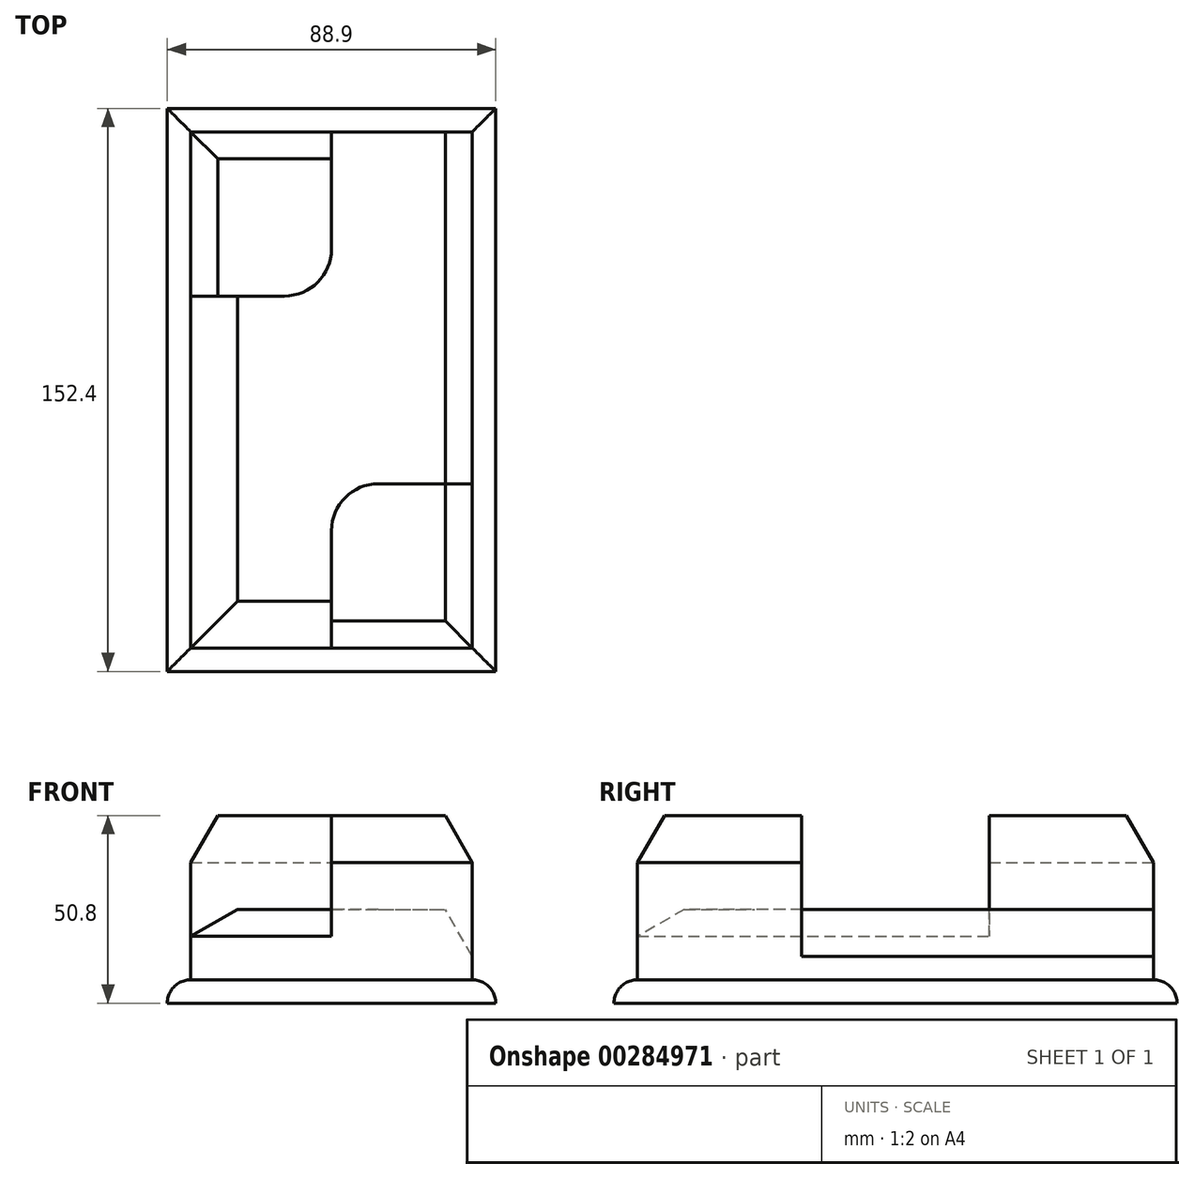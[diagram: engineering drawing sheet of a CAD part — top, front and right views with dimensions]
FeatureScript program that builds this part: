
annotation { "Feature Type Name" : "Feature", "Feature Type Description" : "" }
export const myFeature = defineFeature(function(context is Context, id is Id, definition is map)
    precondition{}
    {
        {
            var Q0;
            Q0=qCreatedBy(makeId("Top.planeOp"),FACE);
            var sketch = newSketch(context, id + "F0", { "sketchPlane" : qUnion([Q0])});
            skLineSegment(sketch, "E0.bottom", {"start": v(-50.87, 68.07) * mm, "end": v(25.33, 68.07) * mm});
            skLineSegment(sketch, "E0.top", {"start": v(-50.87, -71.63) * mm, "end": v(25.33, -71.63) * mm});
            skLineSegment(sketch, "E0.left", {"start": v(-50.87, 68.07) * mm, "end": v(-50.87, -71.63) * mm});
            skLineSegment(sketch, "E0.right", {"start": v(25.33, 68.07) * mm, "end": v(25.33, -71.63) * mm});
            skLineSegment(sketch, "E1.0", {"start": v(-57.22, 74.42) * mm, "end": v(31.68, 74.42) * mm});
            skLineSegment(sketch, "E1.1", {"start": v(-57.22, 74.42) * mm, "end": v(-57.22, -77.98) * mm});
            skLineSegment(sketch, "E1.2", {"start": v(-57.22, -77.98) * mm, "end": v(31.68, -77.98) * mm});
            skLineSegment(sketch, "E1.3", {"start": v(31.68, 74.42) * mm, "end": v(31.68, -77.98) * mm});
            skPoint(sketch, "E2", {"position": v(-12.77, 68.07) * mm});
            skLineSegment(sketch, "E3", {"start": v(-12.77, 68.07) * mm, "end": v(-12.77, 36.32) * mm});
            skLineSegment(sketch, "E4", {"start": v(-25.47, 23.62) * mm, "end": v(-50.87, 23.62) * mm});
            skPoint(sketch, "E5.visualSharp", {"position": v(-12.77, 23.62) * mm});
            skArc(sketch, "E5.filletArc", {"start": v(-25.47, 23.62) * mm, "mid": v(-16.5, 27.34) * mm, "end": v(-12.77, 36.32) * mm});
            skLineSegment(sketch, "E6", {"start": v(-12.77, -71.63) * mm, "end": v(-12.77, -39.88) * mm});
            skLineSegment(sketch, "E7", {"start": v(-0.07, -27.18) * mm, "end": v(25.33, -27.18) * mm});
            skPoint(sketch, "E8.visualSharp", {"position": v(-12.77, -27.18) * mm});
            skArc(sketch, "E8.filletArc", {"start": v(-0.07, -27.18) * mm, "mid": v(-9.05, -30.9) * mm, "end": v(-12.77, -39.88) * mm});
            skSolve(sketch);
        }
        {
            var Q0;
            Q0=makeQuery(id+"F0.imprint","IMPRINT",FACE,{"disambiguationData":[TD([[makeQuery(id+"F0.imprint","IMPRINT",EDGE,{"derivedFrom":sQuery(id+"F0.wireOp",EDGE,"E1.0")}),-1.0]])]});
            extrude(context, id + "F1", {"entities" : qUnion([Q0]), "depth" : 6.35 * mm});
        }
        {
            var Q0;
            {var subQ9=sQuery(id+"F0.wireOp",EDGE,"E3");Q0=makeQuery(id+"F0.imprint","IMPRINT",FACE,{"disambiguationData":[TD([[makeQuery(id+"F0.imprint","IMPRINT",EDGE,{"derivedFrom":subQ9}),1.0]])]});}
            extrude(context, id + "F2", {"entities" : qUnion([Q0]), "operationType" : NewBodyOperationType.ADD, "depth" : 25.4 * mm});
        }
        {
            var Q0;
            {var subQ1=sQuery(id+"F0.wireOp",EDGE,"E3");Q0=makeQuery(id+"F0.imprint","IMPRINT",FACE,{"disambiguationData":[TD([[makeQuery(id+"F0.imprint","IMPRINT",EDGE,{"derivedFrom":subQ1}),-1.0]])]});}
            var Q1;
            {var subQ1=sQuery(id+"F0.wireOp",EDGE,"E6");Q1=makeQuery(id+"F0.imprint","IMPRINT",FACE,{"disambiguationData":[TD([[makeQuery(id+"F0.imprint","IMPRINT",EDGE,{"derivedFrom":subQ1}),-1.0]])]});}
            extrude(context, id + "F3", {"entities" : qUnion([Q0, Q1]), "operationType" : NewBodyOperationType.ADD, "depth" : 50.8 * mm});
        }
        {
            var Q0;
            Q0=makeQuery(id+"F1.opExtrude","CAP_EDGE",EDGE,{"disambiguationData":[OSD([sQuery(id+"F0.wireOp",EDGE,"E1.3")])],"isStart":false});
            var Q1;
            Q1=makeQuery(id+"F1.opExtrude","CAP_EDGE",EDGE,{"disambiguationData":[OSD([sQuery(id+"F0.wireOp",EDGE,"E1.2")])],"isStart":false});
            var Q2;
            Q2=makeQuery(id+"F1.opExtrude","CAP_EDGE",EDGE,{"disambiguationData":[OSD([sQuery(id+"F0.wireOp",EDGE,"E1.1")])],"isStart":false});
            var Q3;
            Q3=makeQuery(id+"F1.opExtrude","CAP_EDGE",EDGE,{"disambiguationData":[OSD([sQuery(id+"F0.wireOp",EDGE,"E1.0")])],"isStart":false});
            fillet(context, id + "F4", {"entities" : qUnion([Q0, Q1, Q2, Q3]), "radius" : 6.35 * mm, "tangentPropagation" : true, "allowEdgeOverflow" : false});
        }
        {
            var Q0;
            Q0=makeQuery(id+"F3.opExtrude","CAP_EDGE",EDGE,{"disambiguationData":[OSD([sQuery(id+"F0.wireOp",EDGE,"E0.right")])],"isStart":false});
            var Q1;
            Q1=makeQuery(id+"F3.opExtrude","CAP_EDGE",EDGE,{"disambiguationData":[OSD([sQuery(id+"F0.wireOp",EDGE,"E0.top")])],"isStart":false});
            var Q2;
            Q2=makeQuery(id+"F2.opExtrude","CAP_EDGE",EDGE,{"disambiguationData":[OSD([sQuery(id+"F0.wireOp",EDGE,"E0.right")])],"isStart":false});
            var Q3;
            Q3=makeQuery(id+"F2.opExtrude","CAP_EDGE",EDGE,{"disambiguationData":[OSD([sQuery(id+"F0.wireOp",EDGE,"E0.top")])],"isStart":false});
            var Q4;
            Q4=makeQuery(id+"F2.opExtrude","CAP_EDGE",EDGE,{"disambiguationData":[OSD([sQuery(id+"F0.wireOp",EDGE,"E0.left")])],"isStart":false});
            var Q5;
            Q5=makeQuery(id+"F3.opExtrude","CAP_EDGE",EDGE,{"disambiguationData":[OSD([sQuery(id+"F0.wireOp",EDGE,"E0.bottom")])],"isStart":false});
            chamfer(context, id + "F5", {"entities" : qUnion([Q0, Q1, Q2, Q3, Q4, Q5]), "chamferType" : ChamferType.OFFSET_ANGLE, "width" : 12.7 * mm, "oppositeDirection" : false, "angle" : 30 * degree, "tangentPropagation" : true});
        }
        {
            var Q0;
            Q0=makeQuery(id+"F3.opExtrude","CAP_EDGE",EDGE,{"disambiguationData":[OSD([sQuery(id+"F0.wireOp",EDGE,"E0.left")])],"isStart":false});
            chamfer(context, id + "F6", {"entities" : qUnion([Q0]), "chamferType" : ChamferType.OFFSET_ANGLE, "width" : 12.7 * mm, "oppositeDirection" : true, "angle" : 30 * degree, "tangentPropagation" : true});
        }
    });
